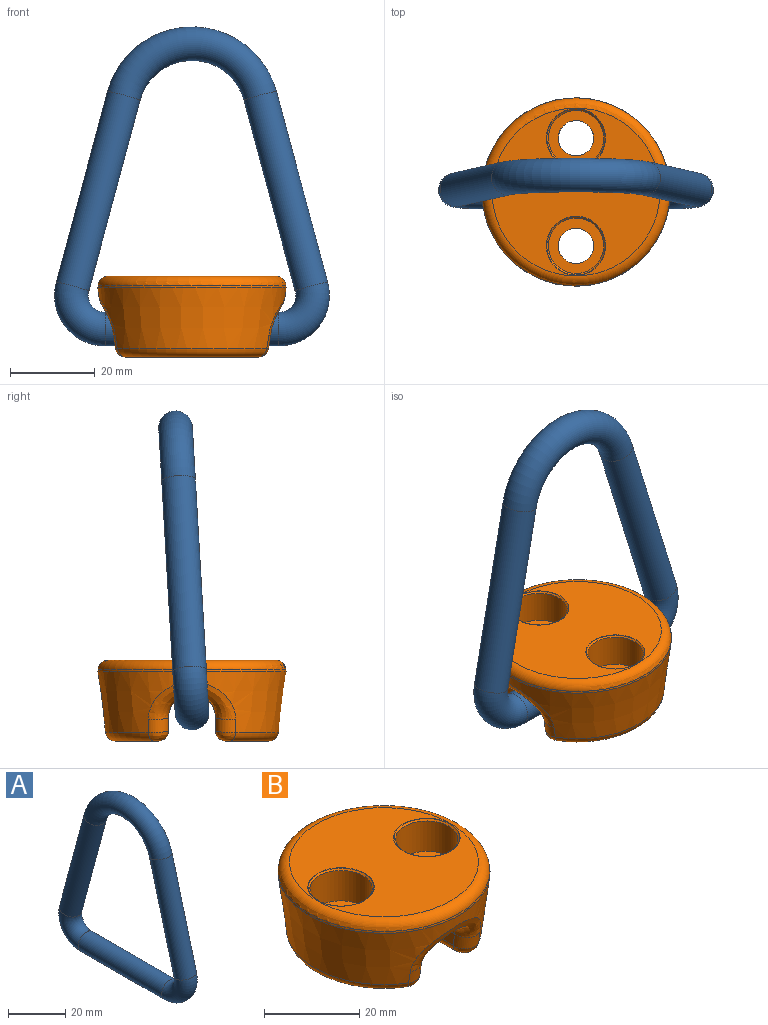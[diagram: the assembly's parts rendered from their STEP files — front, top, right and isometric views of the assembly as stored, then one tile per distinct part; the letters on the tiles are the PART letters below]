
ASSEMBLY  parts=2 mates=1
PART A: 6 faces, bbox 7.9x66.8x78.1 mm
  f0: cylinder r=3.97mm len=47.18mm, axis (0,0.26,0.97), area 1164.9mm2, adj f1,f5
  f1: torus R=7.94mm, axis (-1,0,0), area 362.7mm2, adj f0,f2
  f2: cylinder r=3.97mm len=41.05mm, axis (0,-1,0), area 1023.6mm2, adj f1,f3
  f3: torus R=7.94mm, axis (-1,0,0), area 362.7mm2, adj f2,f4
  f4: cylinder r=3.97mm len=47.18mm, axis (0,0.26,-0.97), area 1164.9mm2, adj f3,f5
  f5: torus R=16.67mm, axis (1,0,0), area 1088.2mm2, adj f0,f4
PART B: 44 faces, bbox 48x48x32 mm
  f0: plane 39.61x39.61mm, normal (0,0,1), area 926.8mm2, adj f22,f42,f43
  f1: cylinder r=5.56mm len=30.74mm, axis (0,1,0), area 274.6mm2, adj f6,f7,f9,f12,f32,f33,f34,f35
  f2: plane 31.44x10.14mm, normal (0,0,-1), area 170mm2, adj f14,f15,f16,f17,f39
  f3: cone r=22.23mm half-angle=7deg, axis (0,0,-1), area 63.1mm2, adj f4,f22
  f4: cone r=22.23mm half-angle=7deg, axis (0,0,1), area 1520.3mm2, adj f3,f8,f9,f10,f11,f12,f13,f16
  f5: plane 31.44x10.14mm, normal (0,0,-1), area 170mm2, adj f18,f19,f20,f21,f38
  f6: plane 30.74x3.18mm, normal (1,0,0), area 96.2mm2, adj f1,f8,f13,f15
  f7: plane 30.74x3.18mm, normal (-1,0,0), area 96.2mm2, adj f1,f10,f11,f20
  f8: bspline ~26.1x8.53mm, area 21mm2, adj f4,f6,f9,f17
  f9: bspline ~20.6x10.49mm, area 128mm2, adj f1,f4,f8,f10
  f10: bspline ~32.03x9.37mm, area 20.9mm2, adj f4,f7,f9,f21
  f11: bspline ~26.1x8.53mm, area 21mm2, adj f4,f7,f12,f18
  f12: bspline ~20.6x10.49mm, area 128mm2, adj f1,f4,f11,f13
  f13: bspline ~32.03x9.37mm, area 20.9mm2, adj f4,f6,f12,f14
  f14: bspline ~5.36x3.34mm, area 16.6mm2, adj f2,f13,f15,f16
  f15: cylinder r=2.39mm len=29.84mm, axis (0,-1,0), area 111.9mm2, adj f2,f6,f14,f17
  f16: torus R=18.09mm, axis (0,0,-1), area 140.7mm2, adj f2,f4,f14,f17
  f17: bspline ~5.37x3.89mm, area 16.6mm2, adj f2,f8,f15,f16
  f18: bspline ~5.37x3.89mm, area 16.6mm2, adj f5,f11,f19,f20
  f19: torus R=18.09mm, axis (0,0,-1), area 140.7mm2, adj f4,f5,f18,f21
  f20: cylinder r=2.39mm len=29.84mm, axis (0,1,0), area 111.9mm2, adj f5,f7,f18,f21
  f21: bspline ~5.36x3.34mm, area 16.6mm2, adj f5,f10,f19,f20
  f22: torus R=19.81mm, axis (0,0,1), area 460.6mm2, adj f0,f3
  f23: cylinder r=6.54mm len=13.08mm, axis (0,0,1), area 320.5mm2, adj f24,f41
  f24: plane 13.08x13.08mm, normal (0,0,1), area 79.9mm2, adj f23,f25
  f25: cylinder r=4.17mm len=10.49mm, axis (0,0,1), area 274.6mm2, adj f24,f38
  f26: cylinder r=6.54mm len=13.08mm, axis (0,0,1), area 320.5mm2, adj f27,f40
  f27: plane 13.08x13.08mm, normal (0,0,1), area 79.9mm2, adj f26,f28
  f28: cylinder r=4.17mm len=10.49mm, axis (0,0,1), area 274.6mm2, adj f27,f39
  f29: cylinder r=5.56mm len=14.86mm, axis (0,-1,0), area 273.5mm2, adj f30,f31,f32,f37
  f30: torus R=5.05mm, axis (0,-1,0), area 7.2mm2, adj f29,f34,f36
  f31: torus R=5.05mm, axis (0,-1,0), area 7.2mm2, adj f29,f33,f35
  f32: cylinder r=0.51mm len=14.86mm, axis (0,1,0), area 1.3mm2, adj f1,f29,f33,f34
  f33: bspline ~5.89x5.61mm, area 5mm2, adj f1,f31,f32,f35
  f34: bspline ~6.89x5.61mm, area 5mm2, adj f1,f30,f32,f36
  f35: bspline ~6.89x5.61mm, area 5mm2, adj f1,f31,f33,f37
  f36: bspline ~6.89x5.61mm, area 5mm2, adj f1,f30,f34,f37
  f37: cylinder r=0.51mm len=14.86mm, axis (0,-1,0), area 1.3mm2, adj f1,f29,f35,f36
  f38: cone r=4.55mm half-angle=45deg, axis (0,0,-1), area 14.7mm2, adj f5,f25
  f39: cone r=4.55mm half-angle=45deg, axis (0,0,-1), area 14.7mm2, adj f2,f28
  f40: cone r=6.54mm half-angle=45deg, axis (0,0,1), area 20.5mm2, adj f26,f43
  f41: cone r=6.54mm half-angle=45deg, axis (0,0,1), area 20.5mm2, adj f23,f42
  f42: torus R=6.97mm, axis (0,0,1), area 4.3mm2, adj f0,f41
  f43: torus R=6.97mm, axis (0,0,1), area 4.3mm2, adj f0,f40
PLACE A rot(axis=(-0.03,-0.03,-1),90deg) t=(0,3.89,73.94)mm
PLACE B rot(axis=(0,0,1),90deg) t=(0,0,16.51)mm fixed
MATE revolute A.f2 <-> B.f29  axis (-1,0,0) through (0,0,6.58)mm
